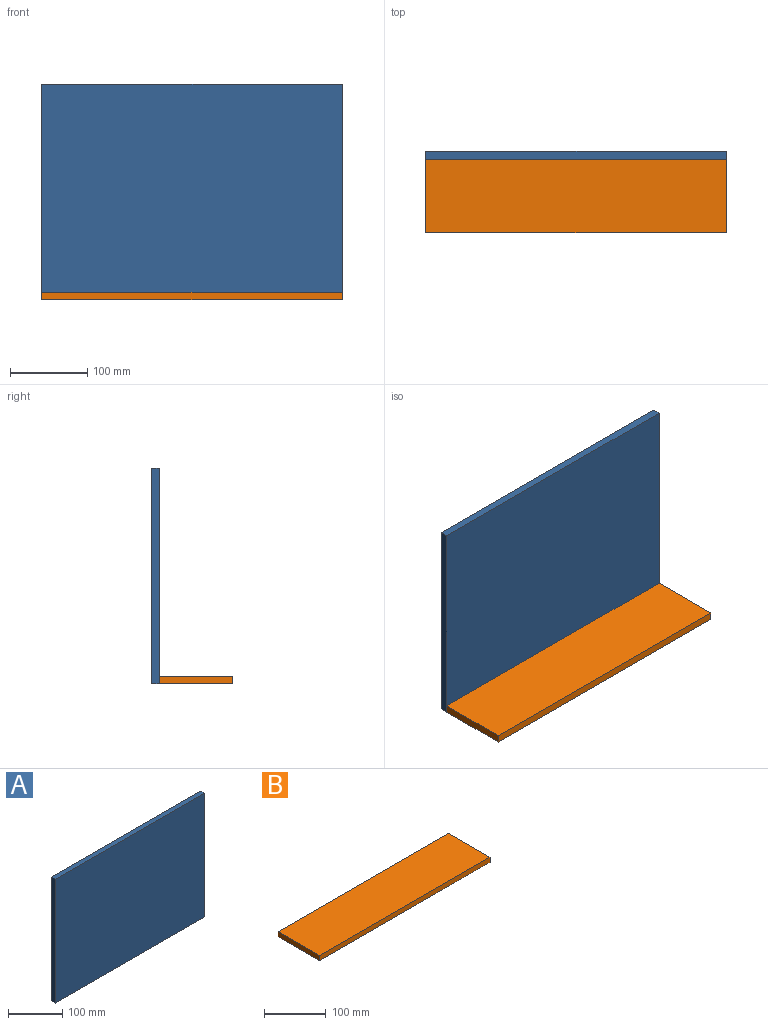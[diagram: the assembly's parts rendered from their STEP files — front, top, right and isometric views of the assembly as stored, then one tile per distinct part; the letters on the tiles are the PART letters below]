
ASSEMBLY  parts=2 mates=1
PART A: 6 faces, bbox 390x10x280 mm
  f0: plane 280x10mm, normal (-1,0,0), area 2800mm2, adj f1,f3,f4,f5
  f1: plane 390x10mm, normal (0,0,-1), area 3900mm2, adj f0,f2,f4,f5
  f2: plane 280x10mm, normal (1,0,0), area 2800mm2, adj f1,f3,f4,f5
  f3: plane 390x10mm, normal (0,0,1), area 3900mm2, adj f0,f2,f4,f5
  f4: plane 390x280mm, normal (0,-1,0), area 109200mm2, adj f0,f1,f2,f3
  f5: plane 390x280mm, normal (0,1,0), area 109200mm2, adj f0,f1,f2,f3
PART B: 6 faces, bbox 390x95x10 mm
  f0: plane 390x10mm, normal (0,1,0), area 3900mm2, adj f1,f3,f4,f5
  f1: plane 95x10mm, normal (-1,0,0), area 950mm2, adj f0,f2,f4,f5
  f2: plane 390x10mm, normal (0,-1,0), area 3900mm2, adj f1,f3,f4,f5
  f3: plane 95x10mm, normal (1,0,0), area 950mm2, adj f0,f2,f4,f5
  f4: plane 390x95mm, normal (0,0,1), area 37050mm2, adj f0,f1,f2,f3
  f5: plane 390x95mm, normal (0,0,-1), area 37050mm2, adj f0,f1,f2,f3
PLACE A t=(28.82,177.25,119.32)mm
PLACE B t=(7.45,125.47,-41.01)mm
MATE fastened A.f4 <-> B.f0  axis (0,-1,0) through (12.46,167.25,-41.01)mm
